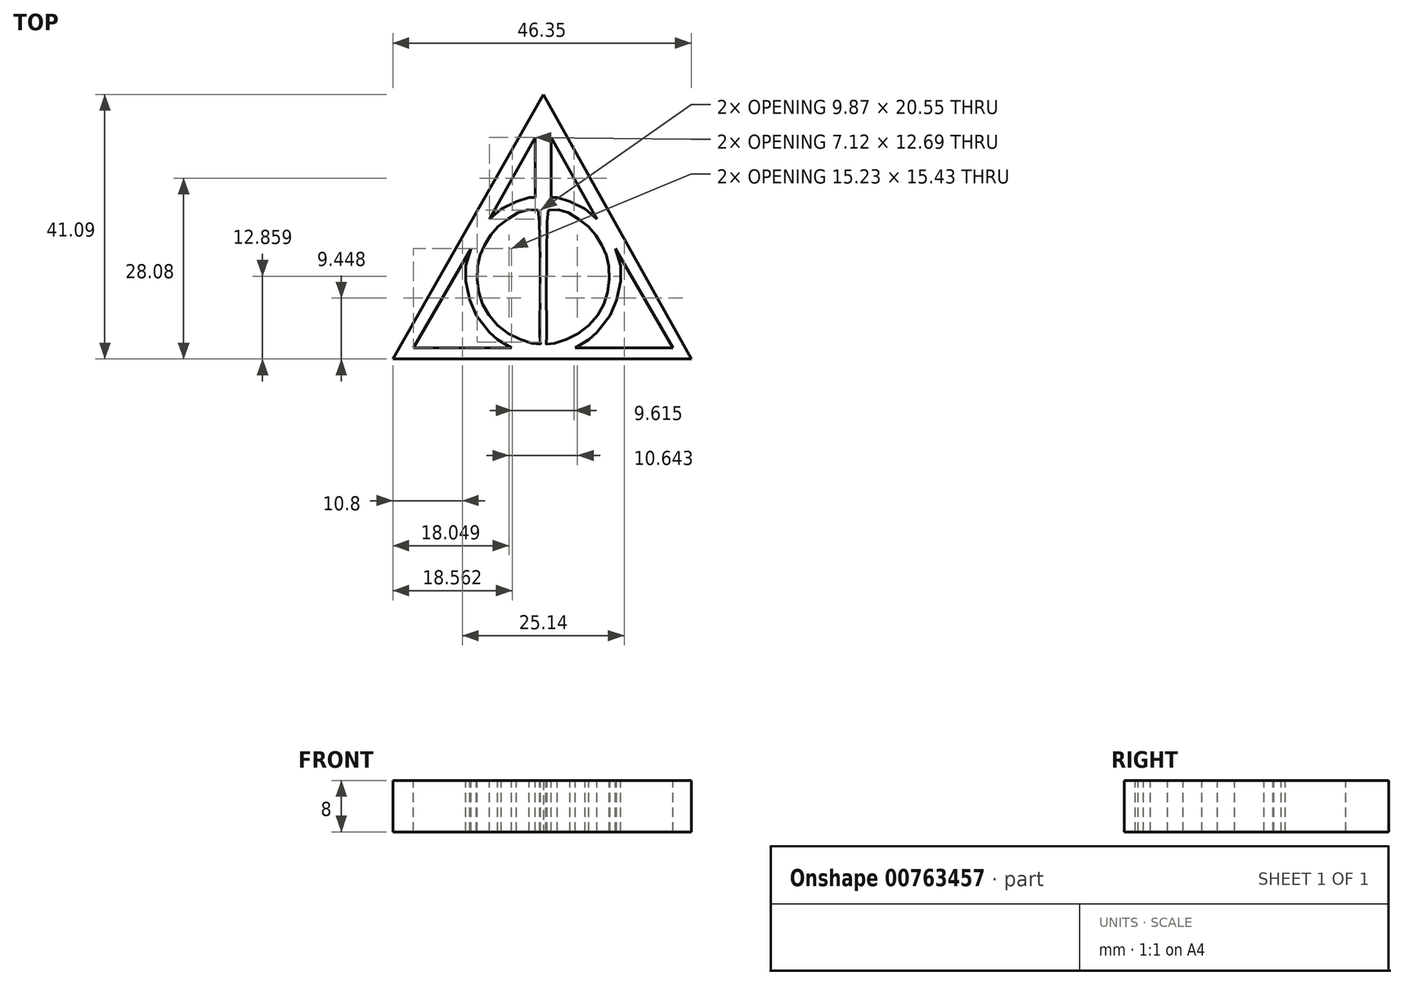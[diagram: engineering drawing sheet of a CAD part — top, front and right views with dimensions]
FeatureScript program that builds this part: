
annotation { "Feature Type Name" : "Feature", "Feature Type Description" : "" }
export const myFeature = defineFeature(function(context is Context, id is Id, definition is map)
    precondition{}
    {
        {
            var Q0;
            Q0=qCreatedBy(makeId("Top.planeOp"),FACE);
            var sketch = newSketch(context, id + "F0", { "sketchPlane" : qUnion([Q0])});
            skLineSegment(sketch, "E0", {"start": v(-25, 43) * mm, "end": v(-48.37, 1.92) * mm});
            skLineSegment(sketch, "E1", {"start": v(-48.37, 1.92) * mm, "end": v(-2.02, 1.92) * mm});
            skLineSegment(sketch, "E2", {"start": v(-2.02, 1.92) * mm, "end": v(-25, 43) * mm});
            skSolve(sketch);
        }
        {
            var Q0;
            Q0 = qSketchRegion(id + "F0", true);
            extrude(context, id + "F1", {"entities" : qUnion([Q0]), "depth" : 8 * mm, "offsetDistance" : 25 * mm});
        }
        {
            var Q0;
            Q0=makeQuery(id+"F1.opExtrude","CAP_FACE",FACE,{"disambiguationData":[OSD([sQuery(id+"F0.wireOp",EDGE,"E0"),sQuery(id+"F0.wireOp",EDGE,"E1"),sQuery(id+"F0.wireOp",EDGE,"E2")])],"isStart":false});
            var sketch = newSketch(context, id + "F2", { "sketchPlane" : qUnion([Q0])});
            skPoint(sketch, "E3.endSnap0", {"position": v(-25.2, 1.92) * mm});
            skLineSegment(sketch, "E4", {"start": v(-26.25, 36.35) * mm, "end": v(-33.37, 23.65) * mm});
            skLineSegment(sketch, "E5", {"start": v(-33.37, 23.65) * mm, "end": v(-31.5, 25.21) * mm});
            skLineSegment(sketch, "E6", {"start": v(-31.5, 25.21) * mm, "end": v(-29.15, 26.35) * mm});
            skLineSegment(sketch, "E7", {"start": v(-29.15, 26.35) * mm, "end": v(-27.2, 27) * mm});
            skLineSegment(sketch, "E8", {"start": v(-27.2, 27) * mm, "end": v(-26.86, 27) * mm});
            skLineSegment(sketch, "E9", {"start": v(-26.86, 27) * mm, "end": v(-26.25, 27) * mm});
            skLineSegment(sketch, "E10", {"start": v(-26.25, 27) * mm, "end": v(-26.25, 36.35) * mm});
            skLineSegment(sketch, "E11", {"start": v(-25, 43) * mm, "end": v(-25, 3.21) * mm});
            skLineSegment(sketch, "E12", {"start": v(-36.21, 19.09) * mm, "end": v(-45.19, 3.65) * mm});
            skLineSegment(sketch, "E13", {"start": v(-45.19, 3.65) * mm, "end": v(-29.96, 3.65) * mm});
            skLineSegment(sketch, "E14", {"start": v(-29.96, 3.65) * mm, "end": v(-32.06, 4.94) * mm});
            skLineSegment(sketch, "E15", {"start": v(-32.06, 4.94) * mm, "end": v(-33.35, 6.03) * mm});
            skLineSegment(sketch, "E16", {"start": v(-33.35, 6.03) * mm, "end": v(-35.4, 8.68) * mm});
            skLineSegment(sketch, "E17", {"start": v(-35.4, 8.68) * mm, "end": v(-36.41, 11.06) * mm});
            skLineSegment(sketch, "E18", {"start": v(-36.41, 11.06) * mm, "end": v(-37.03, 13.99) * mm});
            skLineSegment(sketch, "E19", {"start": v(-37.03, 13.99) * mm, "end": v(-37.03, 16.43) * mm});
            skLineSegment(sketch, "E20", {"start": v(-37.03, 16.43) * mm, "end": v(-36.21, 19.09) * mm});
            skFitSpline(sketch, "E21", {"points": [v(-25.81, 25.05) * mm, v(-27.57, 25.1) * mm, v(-29.35, 24.38) * mm, v(-31.57, 22.89) * mm, v(-33.07, 21.3) * mm, v(-34.32, 19.17) * mm, v(-35.01, 17.46) * mm, v(-35.25, 14.63) * mm, v(-34.9, 11.8) * mm, v(-33.88, 9.41) * mm, v(-31.94, 6.99) * mm, v(-29.43, 5.29) * mm, v(-26.81, 4.37) * mm, v(-25.47, 4.21) * mm, v(-25.5, 5.4) * mm, v(-25.54, 7.9) * mm, v(-25.7, 24.99) * mm, v(-25.81, 25.05) * mm]});
            skLineSegment(sketch, "E22.MirrorCS", {"start": v(-23.75, 36.35) * mm, "end": v(-16.63, 23.65) * mm});
            skLineSegment(sketch, "E23.MirrorCS", {"start": v(-23.75, 27) * mm, "end": v(-23.75, 36.35) * mm});
            skLineSegment(sketch, "E24.MirrorCS", {"start": v(-23.14, 27) * mm, "end": v(-23.75, 27) * mm});
            skLineSegment(sketch, "E25.MirrorCS", {"start": v(-22.8, 27) * mm, "end": v(-23.14, 27) * mm});
            skLineSegment(sketch, "E26.MirrorCS", {"start": v(-20.85, 26.35) * mm, "end": v(-22.8, 27) * mm});
            skLineSegment(sketch, "E27.MirrorCS", {"start": v(-18.5, 25.21) * mm, "end": v(-20.85, 26.35) * mm});
            skLineSegment(sketch, "E28.MirrorCS", {"start": v(-16.63, 23.65) * mm, "end": v(-18.5, 25.21) * mm});
            skFitSpline(sketch, "E29.MirrorC", {"points": [v(-24.19, 25.05) * mm, v(-22.43, 25.1) * mm, v(-20.65, 24.38) * mm, v(-18.43, 22.89) * mm, v(-16.93, 21.3) * mm, v(-15.68, 19.17) * mm, v(-14.99, 17.46) * mm, v(-14.75, 14.63) * mm, v(-15.1, 11.8) * mm, v(-16.12, 9.41) * mm, v(-18.06, 6.99) * mm, v(-20.57, 5.29) * mm, v(-23.19, 4.37) * mm, v(-24.53, 4.21) * mm, v(-24.5, 5.4) * mm, v(-24.46, 7.9) * mm, v(-24.3, 24.99) * mm, v(-24.19, 25.05) * mm]});
            skLineSegment(sketch, "E30.MirrorCS", {"start": v(-13.79, 19.09) * mm, "end": v(-4.81, 3.65) * mm});
            skLineSegment(sketch, "E31.MirrorCS", {"start": v(-4.81, 3.65) * mm, "end": v(-20.04, 3.65) * mm});
            skLineSegment(sketch, "E32.MirrorCS", {"start": v(-20.04, 3.65) * mm, "end": v(-17.94, 4.94) * mm});
            skLineSegment(sketch, "E33.MirrorCS", {"start": v(-17.94, 4.94) * mm, "end": v(-16.65, 6.03) * mm});
            skLineSegment(sketch, "E34.MirrorCS", {"start": v(-16.65, 6.03) * mm, "end": v(-14.6, 8.68) * mm});
            skLineSegment(sketch, "E35.MirrorCS", {"start": v(-14.6, 8.68) * mm, "end": v(-13.59, 11.06) * mm});
            skLineSegment(sketch, "E36.MirrorCS", {"start": v(-13.59, 11.06) * mm, "end": v(-12.97, 13.99) * mm});
            skLineSegment(sketch, "E37.MirrorCS", {"start": v(-12.97, 13.99) * mm, "end": v(-12.97, 16.43) * mm});
            skLineSegment(sketch, "E38.MirrorCS", {"start": v(-12.97, 16.43) * mm, "end": v(-13.79, 19.09) * mm});
            skSolve(sketch);
        }
        {
            var Q0;
            Q0 = qSketchRegion(id + "F2", true);
            extrude(context, id + "F3", {"entities" : qUnion([Q0]), "operationType" : NewBodyOperationType.REMOVE, "oppositeDirection" : true, "depth" : 8 * mm, "offsetDistance" : 25 * mm});
        }
    });
